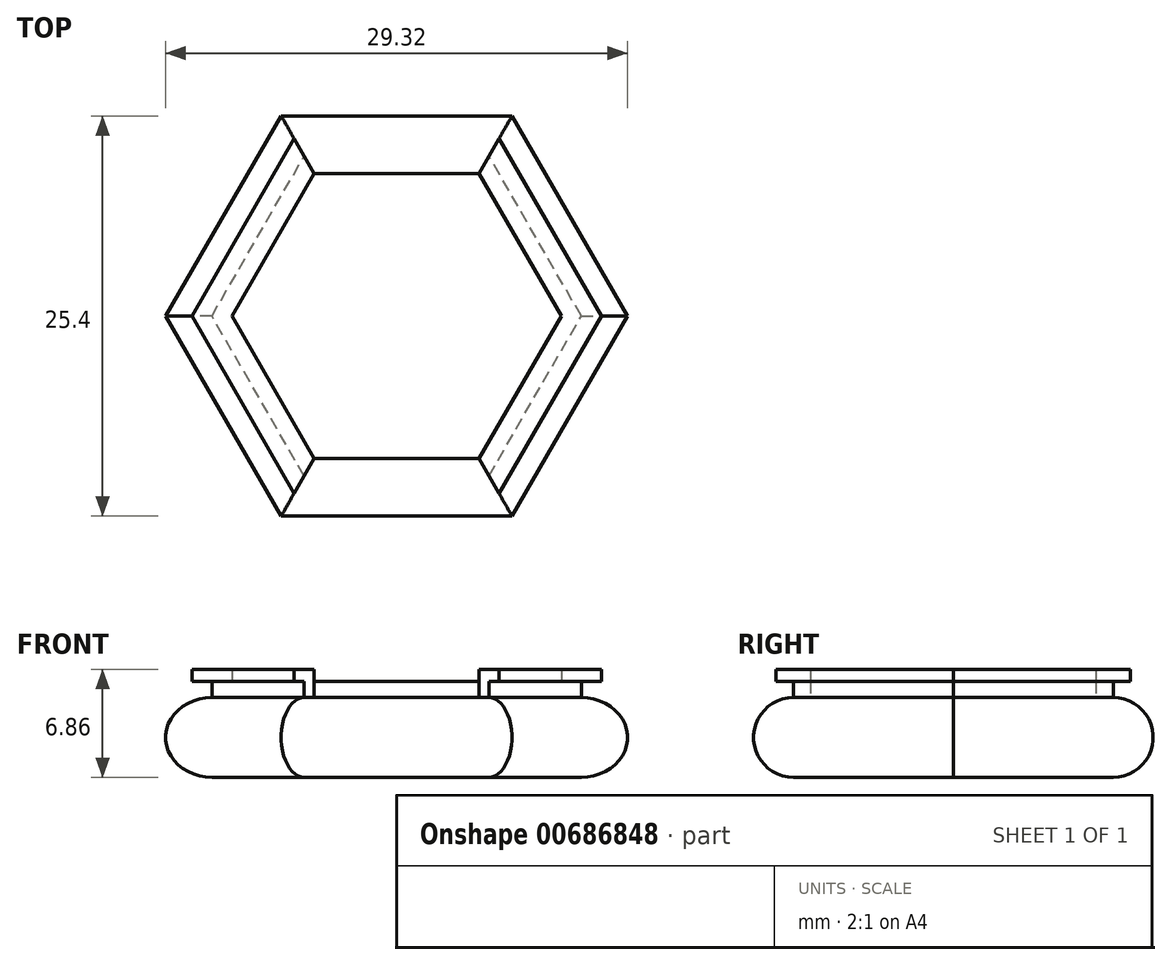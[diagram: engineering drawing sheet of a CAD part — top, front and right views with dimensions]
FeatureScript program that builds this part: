
annotation { "Feature Type Name" : "Feature", "Feature Type Description" : "" }
export const myFeature = defineFeature(function(context is Context, id is Id, definition is map)
    precondition{}
    {
        {
            var Q0;
            Q0=qCreatedBy(makeId("Front.planeOp"),FACE);
            var sketch = newSketch(context, id + "F0", { "sketchPlane" : qUnion([Q0])});
            skLineSegment(sketch, "E0", {"start": v(0, 0) * mm, "end": v(-12.7, 0) * mm});
            skLineSegment(sketch, "E1", {"start": v(-12.7, 0) * mm, "end": v(-12.7, 5.08) * mm, "construction": true});
            skLineSegment(sketch, "E2", {"start": v(12.7, 5.08) * mm, "end": v(12.7, 0) * mm, "construction": true});
            skLineSegment(sketch, "E3", {"start": v(12.7, 0) * mm, "end": v(0, 0) * mm});
            skArc(sketch, "E4", {"start": v(12.7, 0) * mm, "mid": v(15.24, 2.54) * mm, "end": v(12.7, 5.08) * mm});
            skArc(sketch, "E5", {"start": v(-12.7, 5.08) * mm, "mid": v(-15.24, 2.54) * mm, "end": v(-12.7, 0) * mm});
            skLineSegment(sketch, "E6", {"start": v(0, 0) * mm, "end": v(0, 5.08) * mm, "construction": true});
            skLineSegment(sketch, "E7", {"start": v(12.7, 2.54) * mm, "end": v(15.24, 2.54) * mm, "construction": true});
            skLineSegment(sketch, "E8", {"start": v(-12.7, 5.08) * mm, "end": v(12.7, 5.08) * mm});
            skPoint(sketch, "E9", {"position": v(0, 5.08) * mm});
            skSolve(sketch);
        }
        {
            var Q0;
            Q0=qSketchRegion(id+"F0",true);
            extrude(context, id + "F1", {"entities" : qUnion([Q0]), "endBound" : BoundingType.SYMMETRIC, "depth" : 25.4 * mm, "offsetDistance" : 25.4 * mm});
        }
        {
            var Q0;
            Q0=qCreatedBy(makeId("Right.planeOp"),FACE);
            var sketch = newSketch(context, id + "F2", { "sketchPlane" : qUnion([Q0])});
            skLineSegment(sketch, "E10", {"start": v(0, 0) * mm, "end": v(-10.16, 0) * mm, "construction": true});
            skLineSegment(sketch, "E11", {"start": v(0, 0) * mm, "end": v(10.16, 0) * mm, "construction": true});
            skLineSegment(sketch, "E12", {"start": v(-10.16, 0) * mm, "end": v(-10.16, 5.08) * mm, "construction": true});
            skLineSegment(sketch, "E13", {"start": v(10.16, 0) * mm, "end": v(10.16, 5.08) * mm, "construction": true});
            skArc(sketch, "E14", {"start": v(10.16, 0) * mm, "mid": v(12.7, 2.54) * mm, "end": v(10.16, 5.08) * mm});
            skArc(sketch, "E15", {"start": v(-10.16, 5.08) * mm, "mid": v(-12.7, 2.54) * mm, "end": v(-10.16, 0) * mm});
            skLineSegment(sketch, "E16", {"start": v(0, 0) * mm, "end": v(0, 5.08) * mm, "construction": true});
            skLineSegment(sketch, "E17", {"start": v(29.21, 5.08) * mm, "end": v(29.21, 0) * mm});
            skLineSegment(sketch, "E18", {"start": v(-29.21, 5.08) * mm, "end": v(-29.21, 0) * mm});
            skLineSegment(sketch, "E19", {"start": v(-10.16, 0) * mm, "end": v(-29.21, 0) * mm});
            skLineSegment(sketch, "E20", {"start": v(-10.16, 2.54) * mm, "end": v(-12.7, 2.54) * mm, "construction": true});
            skLineSegment(sketch, "E21", {"start": v(29.21, 0) * mm, "end": v(10.16, 0) * mm});
            skLineSegment(sketch, "E22", {"start": v(0, 0) * mm, "end": v(0, 0) * mm});
            skLineSegment(sketch, "E23", {"start": v(10.16, 5.08) * mm, "end": v(-10.16, 5.08) * mm, "construction": true});
            skLineSegment(sketch, "E24", {"start": v(29.21, 5.08) * mm, "end": v(10.16, 5.08) * mm});
            skLineSegment(sketch, "E25", {"start": v(-29.21, 5.08) * mm, "end": v(-10.16, 5.08) * mm});
            skSolve(sketch);
        }
        {
            var Q0;
            Q0=qSketchRegion(id+"F2",true);
            extrude(context, id + "F3", {"entities" : qUnion([Q0]), "operationType" : NewBodyOperationType.REMOVE, "endBound" : BoundingType.SYMMETRIC, "depth" : 50.8 * mm, "offsetDistance" : 25.4 * mm});
        }
        {
            var Q0;
            Q0=sQuery(id+"F0.wireOp",EDGE,"E6");
            cPlane(context, id + "F4", {"entities" : qUnion([Q0]), "cplaneType" : CPlaneType.LINE_ANGLE, "offset" : 25.4 * mm, "angle" : 120 * degree, "width" : 152.4 * mm, "height" : 152.4 * mm});
        }
        {
            var Q0;
            Q0=qCreatedBy(id+"F4.planeOp",FACE);
            var sketch = newSketch(context, id + "F5", { "sketchPlane" : qUnion([Q0])});
            skLineSegment(sketch, "E26", {"start": v(0, 0) * mm, "end": v(-10.16, 0) * mm, "construction": true});
            skLineSegment(sketch, "E27", {"start": v(0, 0) * mm, "end": v(10.16, 0) * mm, "construction": true});
            skLineSegment(sketch, "E28", {"start": v(-10.16, 0) * mm, "end": v(-10.16, 5.08) * mm, "construction": true});
            skLineSegment(sketch, "E29", {"start": v(10.16, 0) * mm, "end": v(10.16, 5.08) * mm, "construction": true});
            skArc(sketch, "E30", {"start": v(10.16, 0) * mm, "mid": v(12.7, 2.54) * mm, "end": v(10.16, 5.08) * mm});
            skArc(sketch, "E31", {"start": v(-10.16, 5.08) * mm, "mid": v(-12.7, 2.54) * mm, "end": v(-10.16, 0) * mm});
            skLineSegment(sketch, "E32", {"start": v(0, 0) * mm, "end": v(0, 5.08) * mm, "construction": true});
            skLineSegment(sketch, "E33", {"start": v(29.21, 5.08) * mm, "end": v(29.21, 0) * mm});
            skLineSegment(sketch, "E34", {"start": v(-29.21, 5.08) * mm, "end": v(-29.21, 0) * mm});
            skLineSegment(sketch, "E35", {"start": v(-10.16, 0) * mm, "end": v(-29.21, 0) * mm});
            skLineSegment(sketch, "E36", {"start": v(-10.16, 2.54) * mm, "end": v(-12.7, 2.54) * mm, "construction": true});
            skLineSegment(sketch, "E37", {"start": v(29.21, 0) * mm, "end": v(10.16, 0) * mm});
            skLineSegment(sketch, "E38", {"start": v(0, 0) * mm, "end": v(0, 0) * mm});
            skLineSegment(sketch, "E39", {"start": v(10.16, 5.08) * mm, "end": v(-10.16, 5.08) * mm, "construction": true});
            skLineSegment(sketch, "E40", {"start": v(29.21, 5.08) * mm, "end": v(10.16, 5.08) * mm});
            skLineSegment(sketch, "E41", {"start": v(-29.21, 5.08) * mm, "end": v(-10.16, 5.08) * mm});
            skSolve(sketch);
        }
        {
            var Q0;
            Q0=qSketchRegion(id+"F5",true);
            var Q1;
            Q1=sQuery(id+"FHUch5MhYWofbFd_1.wireOp",EDGE,"UJUXWhbe-ns99-R938-MBjs-qnEI7qI75ZtX");
            var Q2;
            Q2=sQuery(id+"FHUch5MhYWofbFd_1.wireOp",EDGE,"TGRI2bbO-5mKc-ZYGL-RI2u-ax8UZepCr2S6");
            var Q3;
            Q3=sQuery(id+"FHUch5MhYWofbFd_1.wireOp",EDGE,"3EN97P5a-7fpQ-fkxS-kFIG-O94JdEreBvdc");
            var Q4;
            Q4=sQuery(id+"FHUch5MhYWofbFd_1.wireOp",EDGE,"BLXI86f6-p3FV-xg8e-vcjV-MuaEN1ZbEeBN");
            var Q5;
            Q5=sQuery(id+"FHUch5MhYWofbFd_1.wireOp",EDGE,"K6Pg9hkI-HhUm-eWt8-lgsy-rQcUfMNRkeRX");
            var Q6;
            Q6=sQuery(id+"FHUch5MhYWofbFd_1.wireOp",EDGE,"8MWXePed-qfWZ-9kiI-xQLn-RgFZeWpe4DeW");
            var Q7;
            Q7=sQuery(id+"FHUch5MhYWofbFd_1.wireOp",EDGE,"ujHeR1Bt-oqxH-zWrO-aF7a-1cGxx1oxEC4p");
            var Q8;
            Q8=sQuery(id+"FHUch5MhYWofbFd_1.wireOp",EDGE,"ezDig2bh-fpcZ-qdXg-hfEw-k3bdO8GFTHoY");
            var Q9;
            Q9=sQuery(id+"FHUch5MhYWofbFd_1.wireOp",EDGE,"TL3t9Hpy-tibO-WM6d-k033-ZjCVjvvUcohB");
            var Q10;
            Q10=sQuery(id+"FHUch5MhYWofbFd_1.wireOp",EDGE,"H6XLH3zd-cpDk-JRaX-qujs-Kg6a5HbhHDUq");
            var Q11;
            Q11=sQuery(id+"FHUch5MhYWofbFd_1.wireOp",EDGE,"XlrNxneH-uq2I-L97s-EfPg-StDvBexp0ezL");
            var Q12;
            Q12=sQuery(id+"FHUch5MhYWofbFd_1.wireOp",EDGE,"V9PWrxtB-5fyD-G3Op-kF2t-xwj5HEO20ic1");
            var Q13;
            Q13=sQuery(id+"FHUch5MhYWofbFd_1.wireOp",EDGE,"DBsLzJAx-6rkW-YoXi-OfuC-MLqgEexGkzpa");
            extrude(context, id + "F6", {"entities" : qUnion([Q0]), "operationType" : NewBodyOperationType.REMOVE, "surfaceEntities" : qUnion([Q1, Q2, Q3, Q4, Q5, Q6, Q7, Q8, Q9, Q10, Q11, Q12, Q13]), "endBound" : BoundingType.SYMMETRIC, "oppositeDirection" : true, "depth" : 50.8 * mm, "offsetDistance" : 25.4 * mm});
        }
        {
            var Q0;
            Q0=sQuery(id+"F0.wireOp",EDGE,"E6");
            cPlane(context, id + "F7", {"entities" : qUnion([Q0]), "cplaneType" : CPlaneType.LINE_ANGLE, "offset" : 25.4 * mm, "angle" : 60 * degree, "width" : 152.4 * mm, "height" : 152.4 * mm});
        }
        {
            var Q0;
            Q0=qCreatedBy(id+"F7.planeOp",FACE);
            var sketch = newSketch(context, id + "F8", { "sketchPlane" : qUnion([Q0])});
            skLineSegment(sketch, "E42", {"start": v(0, 0) * mm, "end": v(-10.16, 0) * mm, "construction": true});
            skLineSegment(sketch, "E43", {"start": v(0, 0) * mm, "end": v(10.16, 0) * mm, "construction": true});
            skLineSegment(sketch, "E44", {"start": v(-10.16, 0) * mm, "end": v(-10.16, 5.08) * mm, "construction": true});
            skLineSegment(sketch, "E45", {"start": v(10.16, 0) * mm, "end": v(10.16, 5.08) * mm, "construction": true});
            skArc(sketch, "E46", {"start": v(10.16, 0) * mm, "mid": v(12.7, 2.54) * mm, "end": v(10.16, 5.08) * mm});
            skArc(sketch, "E47", {"start": v(-10.16, 5.08) * mm, "mid": v(-12.7, 2.54) * mm, "end": v(-10.16, 0) * mm});
            skLineSegment(sketch, "E48", {"start": v(0, 0) * mm, "end": v(0, 5.08) * mm, "construction": true});
            skLineSegment(sketch, "E49", {"start": v(29.21, 5.08) * mm, "end": v(29.21, 0) * mm});
            skLineSegment(sketch, "E50", {"start": v(-29.21, 5.08) * mm, "end": v(-29.21, 0) * mm});
            skLineSegment(sketch, "E51", {"start": v(-10.16, 0) * mm, "end": v(-29.21, 0) * mm});
            skLineSegment(sketch, "E52", {"start": v(-10.16, 2.54) * mm, "end": v(-12.7, 2.54) * mm, "construction": true});
            skLineSegment(sketch, "E53", {"start": v(29.21, 0) * mm, "end": v(10.16, 0) * mm});
            skLineSegment(sketch, "E54", {"start": v(0, 0) * mm, "end": v(0, 0) * mm});
            skLineSegment(sketch, "E55", {"start": v(10.16, 5.08) * mm, "end": v(-10.16, 5.08) * mm, "construction": true});
            skLineSegment(sketch, "E56", {"start": v(29.21, 5.08) * mm, "end": v(10.16, 5.08) * mm});
            skLineSegment(sketch, "E57", {"start": v(-29.21, 5.08) * mm, "end": v(-10.16, 5.08) * mm});
            skSolve(sketch);
        }
        {
            var Q0;
            Q0=qSketchRegion(id+"F8",true);
            extrude(context, id + "F9", {"entities" : qUnion([Q0]), "operationType" : NewBodyOperationType.REMOVE, "endBound" : BoundingType.SYMMETRIC, "oppositeDirection" : true, "depth" : 50.8 * mm, "offsetDistance" : 25.4 * mm});
        }
        {
            var Q0;
            Q0=makeQuery(id+"FriaykctB5W3C7Q_1.boolean.opBoolean","SPLIT",FACE,{"disambiguationData":[TD([makeQuery(id+"F6.boolean.opBoolean","COPY",FACE,{"derivedFrom":makeQuery(id+"F6.opExtrude","SWEPT_FACE",FACE,{"disambiguationData":[OSD([sQuery(id+"F5.wireOp",EDGE,"E30")])]})})])],"derivedFrom":makeQuery(id+"F1.opExtrude","SWEPT_FACE",FACE,{"disambiguationData":[OSD([sQuery(id+"F0.wireOp",EDGE,"E8")])]})});
            var sketch = newSketch(context, id + "F10", { "sketchPlane" : qUnion([Q0])});
            skLineSegment(sketch, "E58", {"start": v(5.87, 10.16) * mm, "end": v(6.5, 11.26) * mm});
            skLineSegment(sketch, "E59", {"start": v(6.5, 11.26) * mm, "end": v(13, 0) * mm});
            skLineSegment(sketch, "E60", {"start": v(13, 0) * mm, "end": v(6.5, -11.26) * mm});
            skLineSegment(sketch, "E61", {"start": v(-5.87, 10.16) * mm, "end": v(-6.5, 11.26) * mm});
            skLineSegment(sketch, "E62", {"start": v(-6.5, 11.26) * mm, "end": v(-13, 0) * mm});
            skLineSegment(sketch, "E63", {"start": v(-13, 0) * mm, "end": v(-6.5, -11.26) * mm});
            skLineSegment(sketch, "E64", {"start": v(-6.5, -11.26) * mm, "end": v(-5.87, -10.16) * mm});
            skLineSegment(sketch, "E65", {"start": v(6.5, -11.26) * mm, "end": v(5.87, -10.16) * mm});
            skLineSegment(sketch, "E66", {"start": v(5.23, 9.06) * mm, "end": v(10.46, 0) * mm});
            skLineSegment(sketch, "E67", {"start": v(10.46, 0) * mm, "end": v(5.23, -9.06) * mm});
            skLineSegment(sketch, "E68", {"start": v(5.23, -9.06) * mm, "end": v(5.87, -10.16) * mm});
            skLineSegment(sketch, "E69", {"start": v(0, 0) * mm, "end": v(5.23, 9.06) * mm, "construction": true});
            skLineSegment(sketch, "E70", {"start": v(5.23, 9.06) * mm, "end": v(5.87, 10.16) * mm});
            skLineSegment(sketch, "E71", {"start": v(0, 0) * mm, "end": v(-5.23, 9.06) * mm, "construction": true});
            skLineSegment(sketch, "E72", {"start": v(-5.23, 9.06) * mm, "end": v(-5.87, 10.16) * mm});
            skLineSegment(sketch, "E73", {"start": v(-5.23, 9.06) * mm, "end": v(-10.46, 0) * mm});
            skLineSegment(sketch, "E74", {"start": v(-10.46, 0) * mm, "end": v(-5.23, -9.06) * mm});
            skLineSegment(sketch, "E75", {"start": v(-5.23, -9.06) * mm, "end": v(-5.87, -10.16) * mm});
            skLineSegment(sketch, "E76", {"start": v(-5.23, -9.06) * mm, "end": v(5.23, -9.06) * mm});
            skLineSegment(sketch, "E77", {"start": v(-5.23, 9.06) * mm, "end": v(5.23, 9.06) * mm});
            skSolve(sketch);
        }
        {
            var Q0;
            Q0=makeQuery(id+"F10.imprint","IMPRINT",FACE,{"disambiguationData":[TD([[makeQuery(id+"F10.imprint","IMPRINT",EDGE,{"derivedFrom":sQuery(id+"F10.wireOp",EDGE,"E72")}),1.0]])]});
            var Q1;
            Q1=makeQuery(id+"F10.imprint","IMPRINT",FACE,{"disambiguationData":[TD([[makeQuery(id+"F10.imprint","IMPRINT",EDGE,{"derivedFrom":sQuery(id+"F10.wireOp",EDGE,"E61")}),1.0]])]});
            var Q2;
            Q2=makeQuery(id+"F10.imprint","IMPRINT",FACE,{"disambiguationData":[TD([[makeQuery(id+"F10.imprint","IMPRINT",EDGE,{"derivedFrom":sQuery(id+"F10.wireOp",EDGE,"E66")}),1.0]])]});
            var Q3;
            Q3=makeQuery(id+"F10.imprint","IMPRINT",FACE,{"disambiguationData":[TD([[makeQuery(id+"F10.imprint","IMPRINT",EDGE,{"derivedFrom":sQuery(id+"F10.wireOp",EDGE,"E58")}),-1.0]])]});
            extrude(context, id + "F11", {"entities" : qUnion([Q0, Q1, Q2, Q3]), "operationType" : NewBodyOperationType.ADD, "depth" : 1.78 * mm, "offsetDistance" : 25.4 * mm});
        }
        {
            var Q0;
            Q0=makeQuery(id+"F10.imprint","IMPRINT",FACE,{"disambiguationData":[TD([[makeQuery(id+"F10.imprint","IMPRINT",EDGE,{"derivedFrom":sQuery(id+"F10.wireOp",EDGE,"E58")}),-1.0]])]});
            var Q1;
            Q1=makeQuery(id+"F10.imprint","IMPRINT",FACE,{"disambiguationData":[TD([[makeQuery(id+"F10.imprint","IMPRINT",EDGE,{"derivedFrom":sQuery(id+"F10.wireOp",EDGE,"E61")}),1.0]])]});
            extrude(context, id + "F12", {"entities" : qUnion([Q0, Q1]), "operationType" : NewBodyOperationType.REMOVE, "depth" : 1.02 * mm, "offsetDistance" : 25.4 * mm});
        }
        {
            var Q0;
            Q0=makeQuery(id+"F10.imprint","IMPRINT",FACE,{"disambiguationData":[TD([[makeQuery(id+"F10.imprint","IMPRINT",EDGE,{"derivedFrom":sQuery(id+"F10.wireOp",EDGE,"E66")}),-1.0]])]});
            extrude(context, id + "F13", {"entities" : qUnion([Q0]), "operationType" : NewBodyOperationType.ADD, "depth" : 1.02 * mm, "offsetDistance" : 25.4 * mm});
        }
    });
